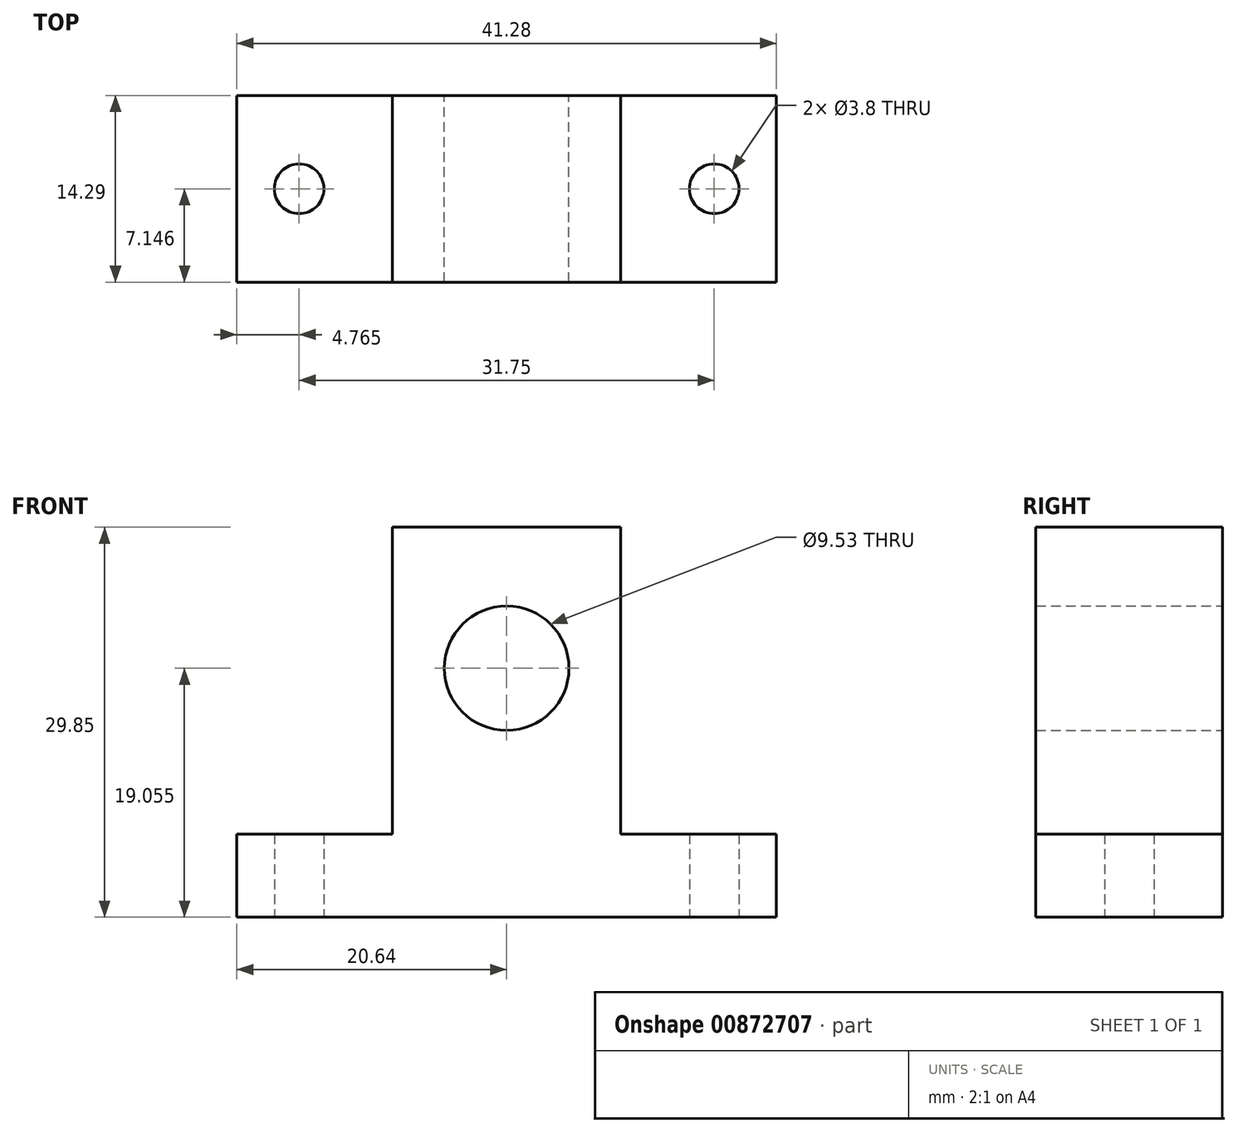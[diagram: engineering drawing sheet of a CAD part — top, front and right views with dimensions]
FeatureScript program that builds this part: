
annotation { "Feature Type Name" : "Feature", "Feature Type Description" : "" }
export const myFeature = defineFeature(function(context is Context, id is Id, definition is map)
    precondition{}
    {
        {
            var Q0;
            Q0=qCreatedBy(makeId("Front.planeOp"),FACE);
            var sketch = newSketch(context, id + "F0", { "sketchPlane" : qUnion([Q0])});
            skLineSegment(sketch, "E0.bottom", {"start": v(20.64, 3.18) * mm, "end": v(-20.64, 3.18) * mm});
            skLineSegment(sketch, "E0.top", {"start": v(20.64, -3.18) * mm, "end": v(-20.64, -3.18) * mm});
            skLineSegment(sketch, "E0.left", {"start": v(20.64, 3.18) * mm, "end": v(20.64, -3.18) * mm});
            skLineSegment(sketch, "E0.right", {"start": v(-20.64, 3.18) * mm, "end": v(-20.64, -3.18) * mm});
            skPoint(sketch, "E0.middle", {"position": v(0, 0) * mm});
            skLineSegment(sketch, "E1.bottom", {"start": v(-8.73, 26.67) * mm, "end": v(8.73, 26.67) * mm});
            skLineSegment(sketch, "E1.top", {"start": v(-8.73, 3.18) * mm, "end": v(8.73, 3.18) * mm});
            skLineSegment(sketch, "E1.left", {"start": v(-8.73, 26.67) * mm, "end": v(-8.73, 3.18) * mm});
            skLineSegment(sketch, "E1.right", {"start": v(8.73, 26.67) * mm, "end": v(8.73, 3.18) * mm});
            skPoint(sketch, "E2", {"position": v(0, 3.18) * mm});
            skCircle(sketch, "E3", {"center": v(0, 15.88) * mm, "radius": 4.76 * mm});
            skPoint(sketch, "E3.centerSnap0", {"position": v(0, 26.67) * mm});
            skSolve(sketch);
        }
        {
            var Q0;
            Q0=makeQuery(id+"F0.imprint","IMPRINT",FACE,{"disambiguationData":[TD([[makeQuery(id+"F0.imprint","IMPRINT",EDGE,{"derivedFrom":sQuery(id+"F0.wireOp",EDGE,"E1.bottom")}),-1.0]])]});
            var Q1;
            Q1=makeQuery(id+"F0.imprint","IMPRINT",FACE,{"disambiguationData":[TD([[makeQuery(id+"F0.imprint","IMPRINT",EDGE,{"derivedFrom":sQuery(id+"F0.wireOp",EDGE,"E0.top")}),-1.0]])]});
            extrude(context, id + "F1", {"entities" : qUnion([Q0, Q1]), "depth" : 14.29 * mm, "offsetDistance" : 25.4 * mm});
        }
        {
            var Q0;
            Q0=makeQuery(id+"F1.opExtrude","SWEPT_FACE",FACE,{"disambiguationData":[OSD([sQuery(id+"F0.wireOp",EDGE,"E0.top")])]});
            var sketch = newSketch(context, id + "F2", { "sketchPlane" : qUnion([Q0])});
            skCircle(sketch, "E4", {"center": v(-15.88, 7.14) * mm, "radius": 1.59 * mm});
            skPoint(sketch, "E4.centerSnap0", {"position": v(-20.64, 7.14) * mm});
            skCircle(sketch, "E5.MirrorC", {"center": v(15.88, 7.14) * mm, "radius": 1.59 * mm});
            skSolve(sketch);
        }
        {
            var Q0;
            Q0=sQuery(id+"F2.wireOp",VERTEX,"E4.center");
            var Q1;
            Q1=sQuery(id+"F2.wireOp",VERTEX,"E5.MirrorC.center");
            var Q2;
            Q2=makeQuery(id+"F1.opExtrude","SWEPT_BODY",BODY,{"disambiguationData":[OSD([sQuery(id+"F0.wireOp",EDGE,"E0.bottom"),sQuery(id+"F0.wireOp",EDGE,"E0.top"),sQuery(id+"F0.wireOp",EDGE,"E0.left"),sQuery(id+"F0.wireOp",EDGE,"E0.right"),sQuery(id+"F0.wireOp",EDGE,"E1.bottom"),sQuery(id+"F0.wireOp",EDGE,"E1.left"),sQuery(id+"F0.wireOp",EDGE,"E1.right"),sQuery(id+"F0.wireOp",EDGE,"E3")])]});
            hole(context, id + "F3", {"style" : HoleStyle.SIMPLE, "endStyle" : HoleEndStyle.THROUGH, "standardTappedOrClearance" : lookupTablePath({ "fit" : "Normal (ASME)", "standard" : "ANSI", "size" : "#6", "type" : "Clearance" }), "standardBlindInLast" : lookupTablePath({ "fit" : "Free", "standard" : "ANSI", "size" : "#6", "type" : "Clearance" }), "holeDiameter" : 3.8 * mm, "majorDiameter" : 6.35 * mm, "isTappedThrough" : true, "tappedDepth" : 12.7 * mm, "tapClearance" : 3, "locations" : qUnion([Q0, Q1]), "scope" : qUnion([Q2])});
        }
    });
